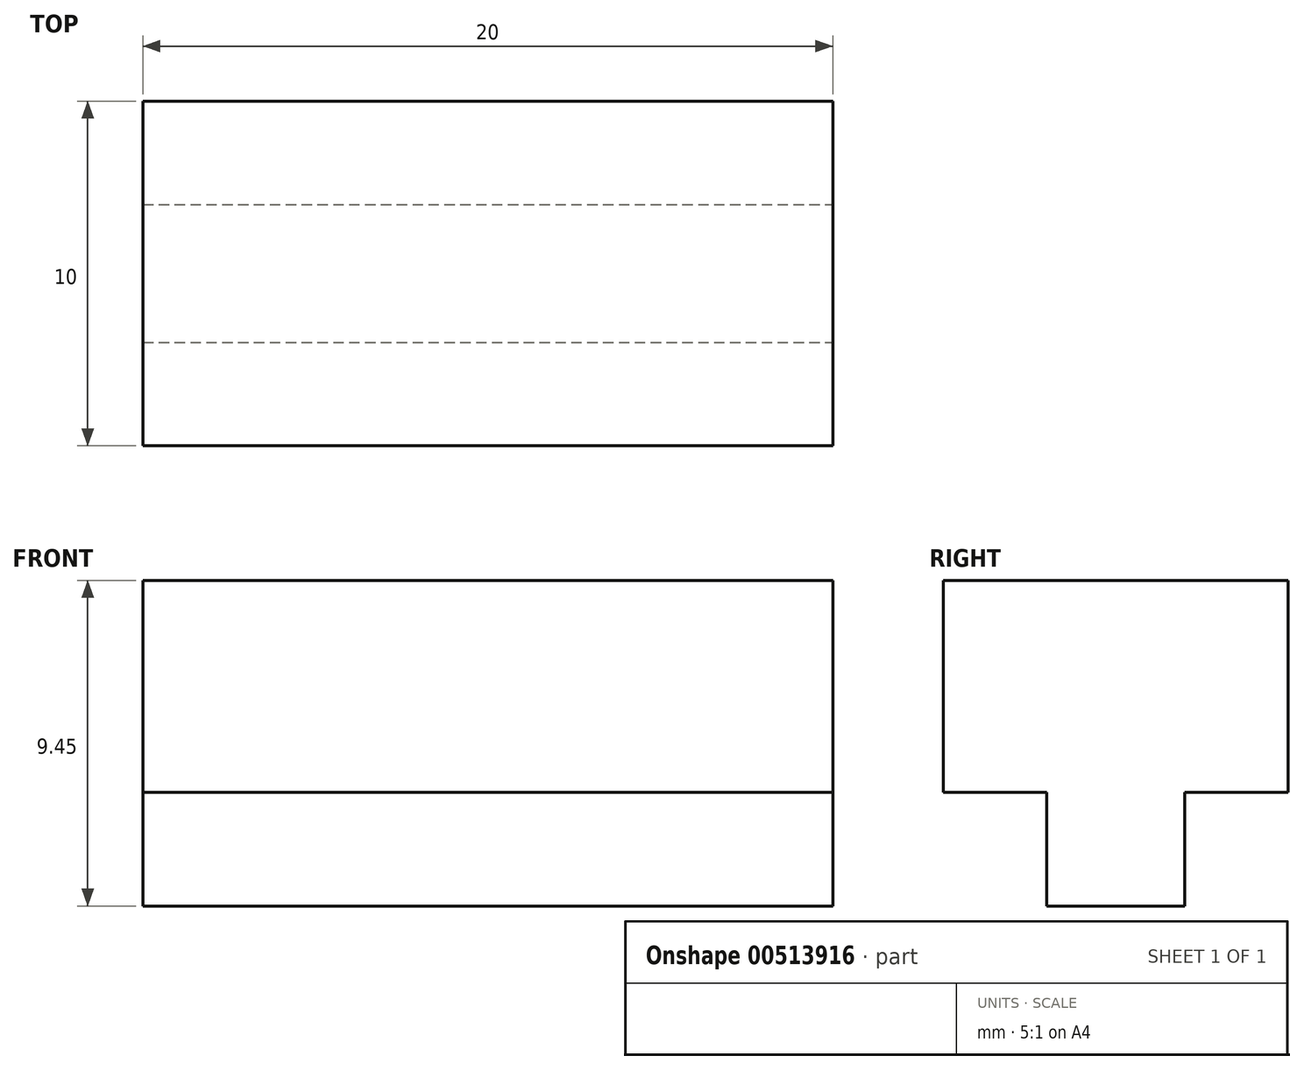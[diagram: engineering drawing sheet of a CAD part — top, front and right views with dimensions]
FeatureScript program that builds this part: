
annotation { "Feature Type Name" : "Feature", "Feature Type Description" : "" }
export const myFeature = defineFeature(function(context is Context, id is Id, definition is map)
    precondition{}
    {
        {
            var Q0;
            Q0=qCreatedBy(makeId("Front.planeOp"),FACE);
            var sketch = newSketch(context, id + "F0", { "sketchPlane" : qUnion([Q0])});
            skLineSegment(sketch, "E0", {"start": v(0, 0) * mm, "end": v(20, 0) * mm});
            skLineSegment(sketch, "E1", {"start": v(0, 0) * mm, "end": v(0, 9.45) * mm});
            skLineSegment(sketch, "E2", {"start": v(0, 9.45) * mm, "end": v(20, 9.45) * mm});
            skLineSegment(sketch, "E3", {"start": v(20, 9.45) * mm, "end": v(20, 0) * mm});
            skSolve(sketch);
        }
        {
            var Q0;
            Q0=makeQuery(id+"F0.imprint","IMPRINT",FACE,{"disambiguationData":[TD([[makeQuery(id+"F0.imprint","IMPRINT",EDGE,{"derivedFrom":sQuery(id+"F0.wireOp",EDGE,"E0")}),1.0]])]});
            extrude(context, id + "F1", {"entities" : qUnion([Q0]), "depth" : 10 * mm});
        }
        {
            var Q0;
            Q0=qCreatedBy(makeId("Top.planeOp"),FACE);
            var sketch = newSketch(context, id + "F2", { "sketchPlane" : qUnion([Q0])});
            skLineSegment(sketch, "E4", {"start": v(0, 0) * mm, "end": v(0, -5) * mm});
            skLineSegment(sketch, "E5", {"start": v(0, -5) * mm, "end": v(0, -3) * mm});
            skLineSegment(sketch, "E6", {"start": v(0, -5) * mm, "end": v(0, -7) * mm});
            skLineSegment(sketch, "E7.bottom", {"start": v(0, -3) * mm, "end": v(20, -3) * mm});
            skLineSegment(sketch, "E7.top", {"start": v(0, -7) * mm, "end": v(20, -7) * mm});
            skLineSegment(sketch, "E7.left", {"start": v(0, -3) * mm, "end": v(0, -7) * mm});
            skLineSegment(sketch, "E7.right", {"start": v(20, -3) * mm, "end": v(20, -7) * mm});
            skLineSegment(sketch, "E8.top", {"start": v(0, 0) * mm, "end": v(20, 0) * mm});
            skLineSegment(sketch, "E8.left", {"start": v(0, -3) * mm, "end": v(0, 0) * mm});
            skLineSegment(sketch, "E8.right", {"start": v(20, -3) * mm, "end": v(20, 0) * mm});
            skLineSegment(sketch, "E9.top", {"start": v(0, -10) * mm, "end": v(20, -10) * mm});
            skLineSegment(sketch, "E9.left", {"start": v(0, -7) * mm, "end": v(0, -10) * mm});
            skLineSegment(sketch, "E9.right", {"start": v(20, -7) * mm, "end": v(20, -10) * mm});
            skSolve(sketch);
        }
        {
            var Q0;
            Q0=makeQuery(id+"F2.imprint","IMPRINT",FACE,{"disambiguationData":[TD([[makeQuery(id+"F2.imprint","IMPRINT",EDGE,{"derivedFrom":sQuery(id+"F2.wireOp",EDGE,"E7.top")}),-1.0]])]});
            var Q1;
            Q1=makeQuery(id+"F2.imprint","IMPRINT",FACE,{"disambiguationData":[TD([[makeQuery(id+"F2.imprint","IMPRINT",EDGE,{"derivedFrom":sQuery(id+"F2.wireOp",EDGE,"E7.bottom")}),1.0]])]});
            extrude(context, id + "F3", {"entities" : qUnion([Q0, Q1]), "operationType" : NewBodyOperationType.REMOVE, "depth" : 3.3 * mm});
        }
    });
